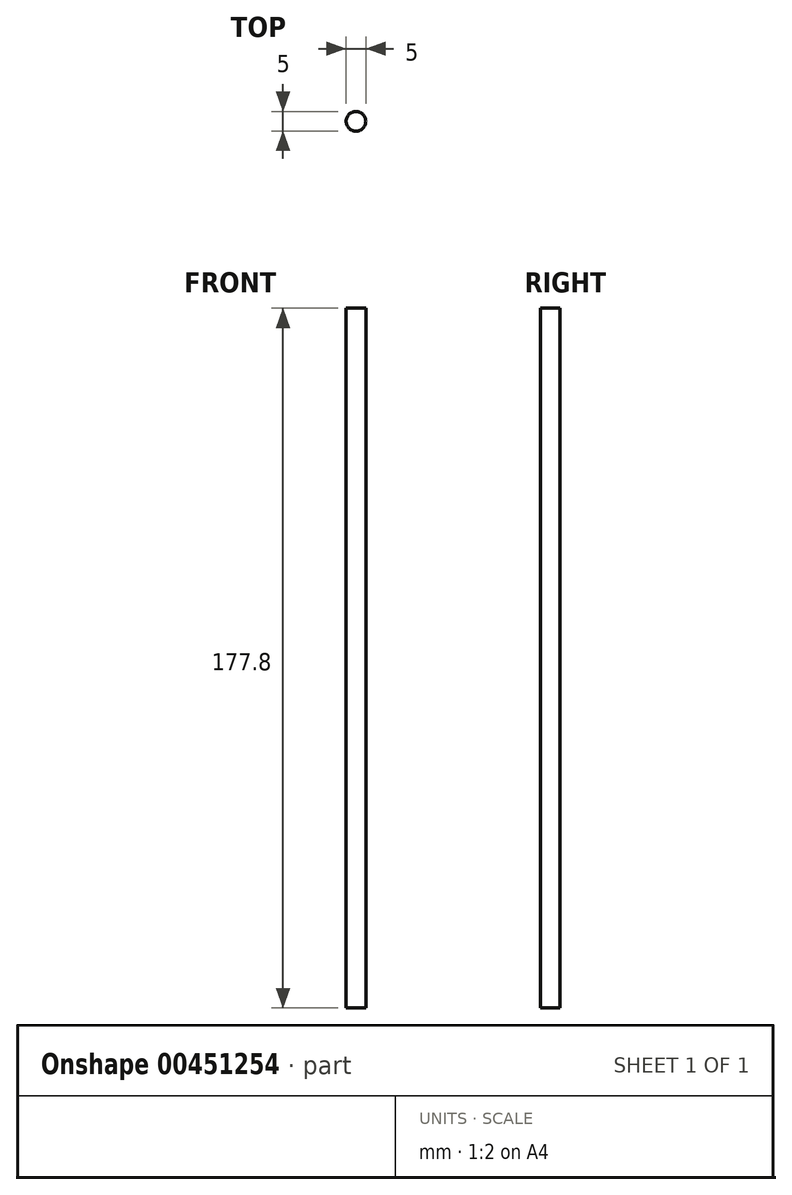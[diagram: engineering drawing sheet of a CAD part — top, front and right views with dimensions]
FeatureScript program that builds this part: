
annotation { "Feature Type Name" : "Feature", "Feature Type Description" : "" }
export const myFeature = defineFeature(function(context is Context, id is Id, definition is map)
    precondition{}
    {
        {
            var Q0;
            Q0=qCreatedBy(makeId("Top.planeOp"),FACE);
            var sketch = newSketch(context, id + "F0", { "sketchPlane" : qUnion([Q0])});
            skCircle(sketch, "E0", {"center": v(0, 0) * mm, "radius": 2.5 * mm});
            skSolve(sketch);
        }
        {
            var Q0;
            Q0 = qSketchRegion(id + "F0", true);
            extrude(context, id + "F1", {"entities" : qUnion([Q0]), "endBound" : BoundingType.SYMMETRIC, "depth" : 177.8 * mm});
        }
    });
